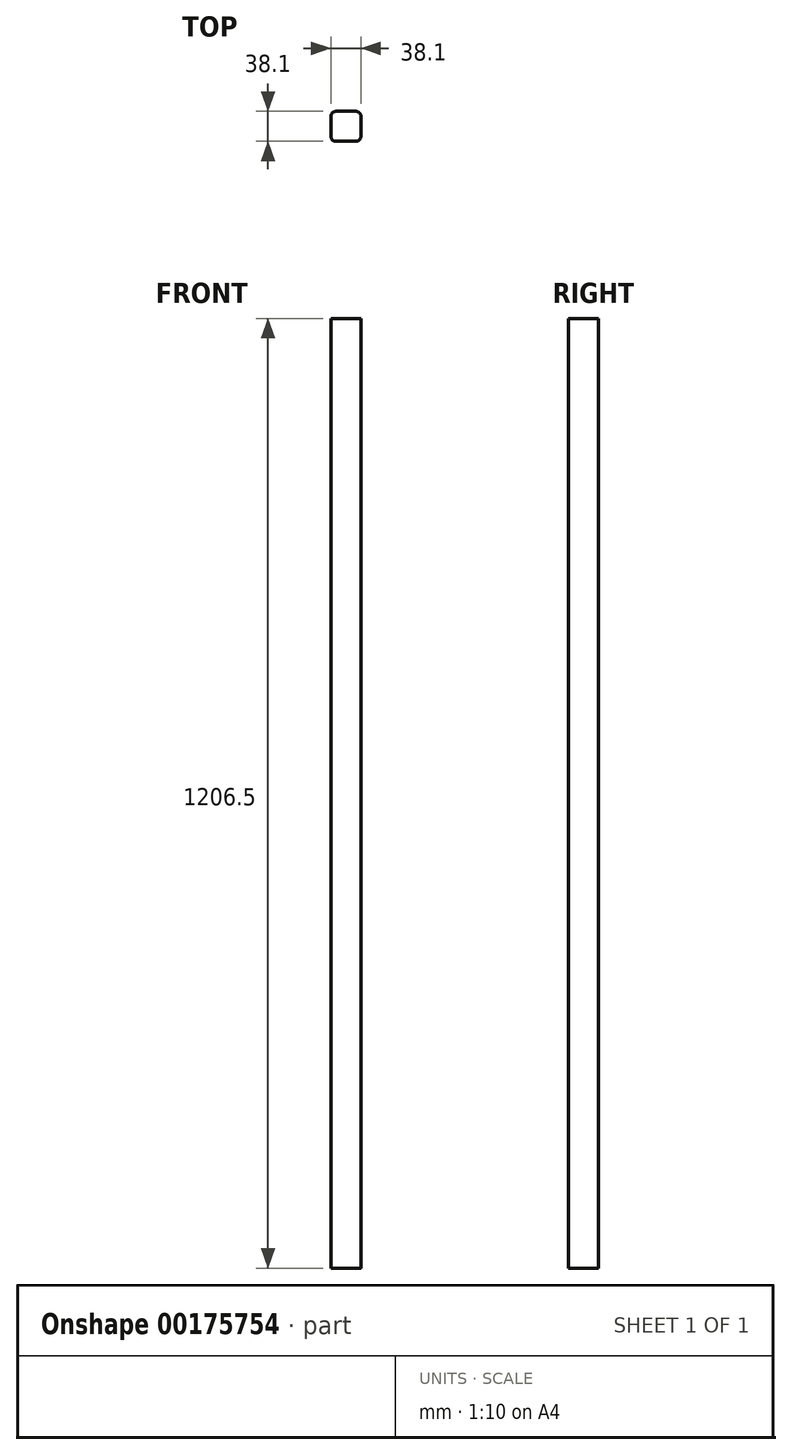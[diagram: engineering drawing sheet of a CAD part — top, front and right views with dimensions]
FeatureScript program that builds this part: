
annotation { "Feature Type Name" : "Feature", "Feature Type Description" : "" }
export const myFeature = defineFeature(function(context is Context, id is Id, definition is map)
    precondition{}
    {
        {
            var Q0;
            Q0=qCreatedBy(makeId("Top.planeOp"),FACE);
            var sketch = newSketch(context, id + "F0", { "sketchPlane" : qUnion([Q0])});
            skLineSegment(sketch, "E0.bottom", {"start": v(12.7, 19.05) * mm, "end": v(-12.7, 19.05) * mm});
            skLineSegment(sketch, "E0.top", {"start": v(12.7, -19.05) * mm, "end": v(-12.7, -19.05) * mm});
            skLineSegment(sketch, "E0.left", {"start": v(19.05, 12.7) * mm, "end": v(19.05, -12.7) * mm});
            skLineSegment(sketch, "E0.right", {"start": v(-19.05, 12.7) * mm, "end": v(-19.05, -12.7) * mm});
            skPoint(sketch, "E0.middle", {"position": v(0, 0) * mm});
            skPoint(sketch, "E1.visualSharp", {"position": v(-19.05, 19.05) * mm});
            skArc(sketch, "E1.filletArc", {"start": v(-12.7, 19.05) * mm, "mid": v(-17.2, 17.2) * mm, "end": v(-19.05, 12.7) * mm});
            skPoint(sketch, "E2.visualSharp", {"position": v(19.05, 19.05) * mm});
            skArc(sketch, "E2.filletArc", {"start": v(19.05, 12.7) * mm, "mid": v(17.2, 17.2) * mm, "end": v(12.7, 19.05) * mm});
            skPoint(sketch, "E3.visualSharp", {"position": v(19.05, -19.05) * mm});
            skArc(sketch, "E3.filletArc", {"start": v(12.7, -19.05) * mm, "mid": v(17.2, -17.2) * mm, "end": v(19.05, -12.7) * mm});
            skPoint(sketch, "E4.visualSharp", {"position": v(-19.05, -19.05) * mm});
            skArc(sketch, "E4.filletArc", {"start": v(-19.05, -12.7) * mm, "mid": v(-17.2, -17.2) * mm, "end": v(-12.7, -19.05) * mm});
            skSolve(sketch);
        }
        {
            var Q0;
            Q0=qSketchRegion(id+"F0",true);
            extrude(context, id + "F1", {"entities" : qUnion([Q0]), "depth" : 1206.5 * mm, "offsetDistance" : 25.4 * mm});
        }
    });
